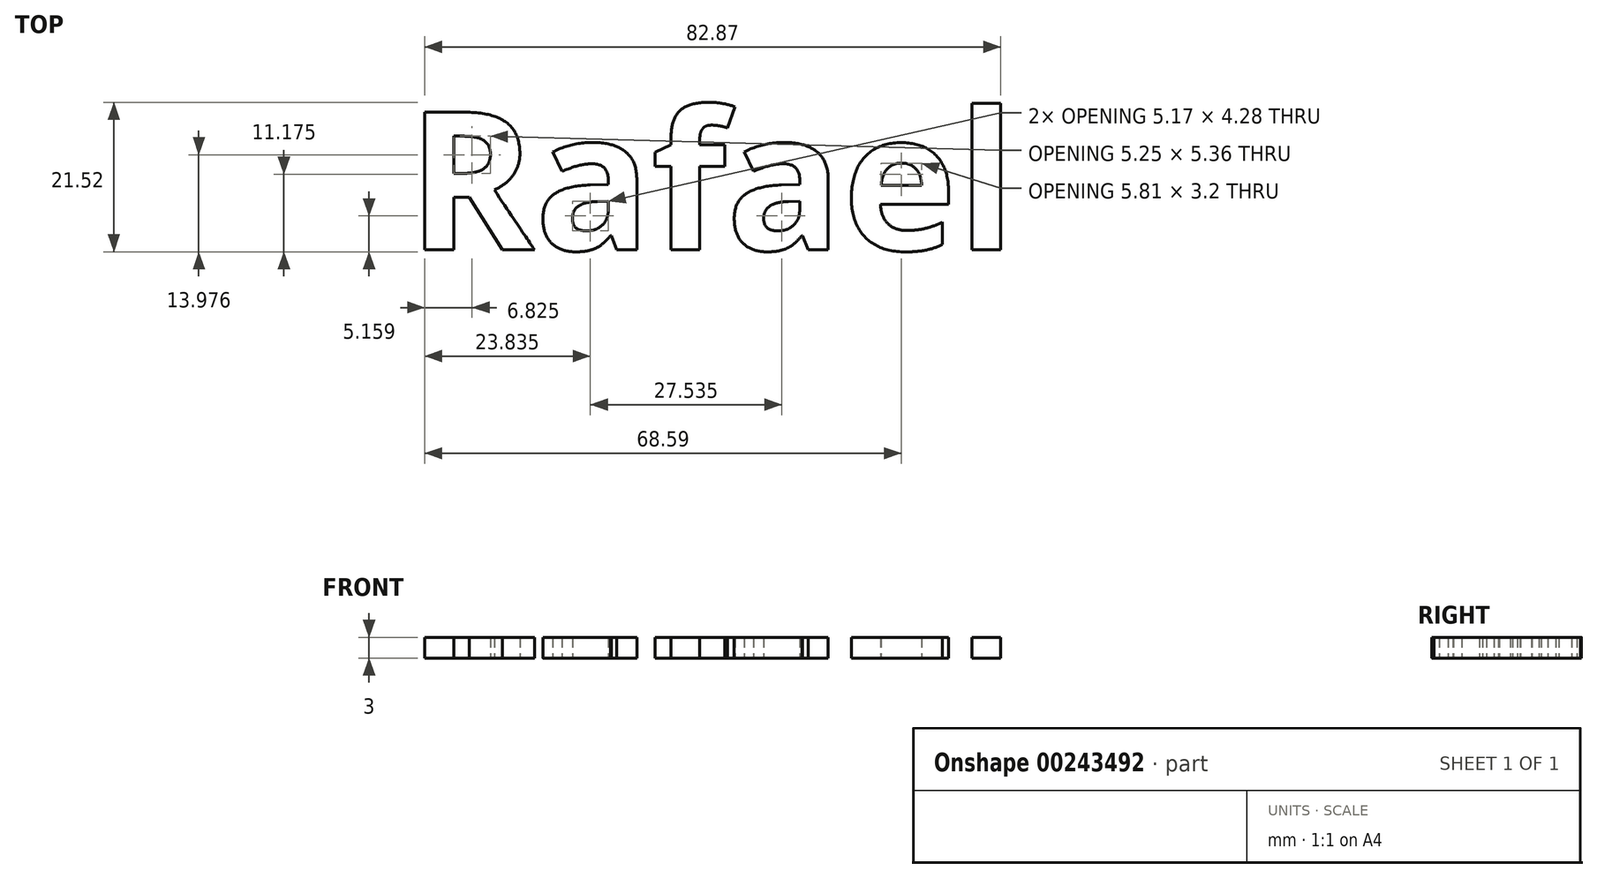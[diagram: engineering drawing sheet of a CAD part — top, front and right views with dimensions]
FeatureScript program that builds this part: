
annotation { "Feature Type Name" : "Feature", "Feature Type Description" : "" }
export const myFeature = defineFeature(function(context is Context, id is Id, definition is map)
    precondition{}
    {
        {
            var Q0;
            Q0=qCreatedBy(makeId("Top.planeOp"),FACE);
            var sketch = newSketch(context, id + "F0", { "sketchPlane" : qUnion([Q0])});
            skText(sketch, "E0", { "text": "Rafael", "fontName": "OpenSans-Bold.ttf"});
            const initialGuessF0  = {"E0": [-0.03216, -0.0099, 1, 0, 0.02]};
            skSetInitialGuess(sketch, initialGuessF0);
            skSolve(sketch);
        }
        {
            var Q0;
            Q0 = qSketchRegion(id + "F0", true);
            extrude(context, id + "F1", {"entities" : qUnion([Q0]), "offsetDistance" : 25 * mm, "depth" : 3 * mm});
        }
    });
